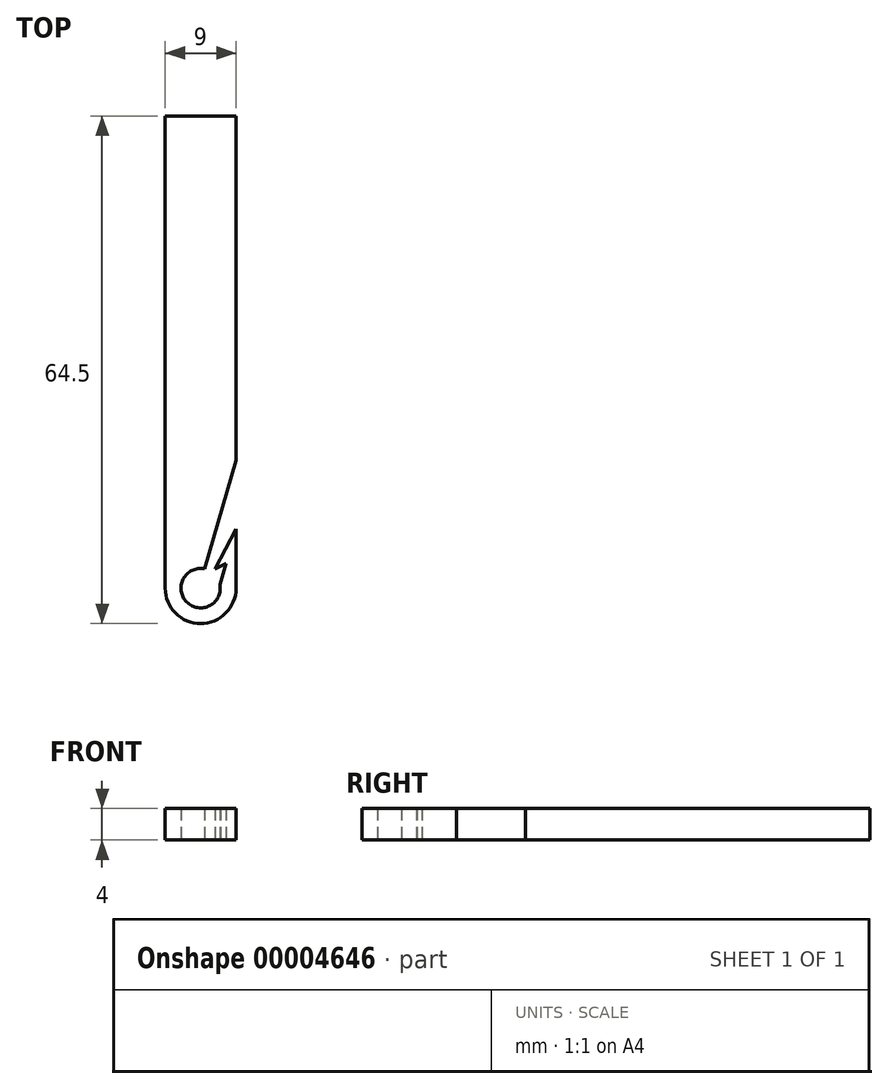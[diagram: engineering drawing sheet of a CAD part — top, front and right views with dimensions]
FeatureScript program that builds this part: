
annotation { "Feature Type Name" : "Feature", "Feature Type Description" : "" }
export const myFeature = defineFeature(function(context is Context, id is Id, definition is map)
    precondition{}
    {
        {
            var Q0;
            Q0=qCreatedBy(makeId("Top.planeOp"),FACE);
            var sketch = newSketch(context, id + "F0", { "sketchPlane" : qUnion([Q0])});
            skCircle(sketch, "E0", {"center": v(0, 0) * mm, "radius": 4.5 * mm});
            skCircle(sketch, "E1.0", {"center": v(0, 0) * mm, "radius": 2.5 * mm});
            skLineSegment(sketch, "E2", {"start": v(-4.5, 0) * mm, "end": v(-4.5, 60) * mm});
            skLineSegment(sketch, "E3", {"start": v(-4.5, 60) * mm, "end": v(4.5, 60) * mm});
            skLineSegment(sketch, "E4", {"start": v(4.5, 0) * mm, "end": v(4.5, 60) * mm});
            skLineSegment(sketch, "E5", {"start": v(0.47, 2.46) * mm, "end": v(4.5, 16.24) * mm});
            skLineSegment(sketch, "E6", {"start": v(1.8, -1.73) * mm, "end": v(4.5, 7.5) * mm});
            skLineSegment(sketch, "E7", {"start": v(3.23, 3.14) * mm, "end": v(1.8, 2.43) * mm});
            skLineSegment(sketch, "E8", {"start": v(1.8, 2.43) * mm, "end": v(4.5, 7.5) * mm});
            skSolve(sketch);
        }
        {
            var Q0;
            {var subQ6=sQuery(id+"F0.wireOp",EDGE,"E2");Q0=makeQuery(id+"F0.imprint","IMPRINT",FACE,{"disambiguationData":[TD([[makeQuery(id+"F0.imprint","IMPRINT",EDGE,{"derivedFrom":subQ6}),-1.0]])]});}
            var Q1;
            {var subQ3=sQuery(id+"F0.wireOp",EDGE,"E0");var subQ10=makeQuery(id+"F0.imprint","INTERSECT",VERTEX,{"derivedFrom":[subQ3,sQuery(id+"F0.wireOp",EDGE,"E2")]});Q1=makeQuery(id+"F0.imprint","IMPRINT",FACE,{"disambiguationData":[TD([[makeQuery(id+"F0.imprint","IMPRINT",EDGE,{"disambiguationData":[TD([[subQ10,1.0]])],"derivedFrom":subQ3}),1.0]])]});}
            var Q2;
            {var subQ1=sQuery(id+"F0.wireOp",EDGE,"E0");var subQ3=sQuery(id+"F0.wireOp",EDGE,"E4");var subQ5=makeQuery(id+"F0.imprint","INTERSECT",VERTEX,{"derivedFrom":[subQ1,subQ3]});Q2=makeQuery(id+"F0.imprint","IMPRINT",FACE,{"disambiguationData":[TD([[makeQuery(id+"F0.imprint","IMPRINT",EDGE,{"disambiguationData":[TD([[subQ5,-1.0]])],"derivedFrom":subQ1}),-1.0]])]});}
            var Q3;
            {var subQ0=sQuery(id+"F0.wireOp",EDGE,"E8");var subQ1=sQuery(id+"F0.wireOp",EDGE,"E0");var subQ2=makeQuery(id+"F0.imprint","INTERSECT",VERTEX,{"derivedFrom":[subQ1,subQ0]});Q3=makeQuery(id+"F0.imprint","IMPRINT",FACE,{"disambiguationData":[TD([[makeQuery(id+"F0.imprint","IMPRINT",EDGE,{"disambiguationData":[TD([[subQ2,1.0]])],"derivedFrom":subQ1}),-1.0]])]});}
            var Q4;
            {var subQ3=sQuery(id+"F0.wireOp",EDGE,"E7");Q4=makeQuery(id+"F0.imprint","IMPRINT",FACE,{"disambiguationData":[TD([[makeQuery(id+"F0.imprint","IMPRINT",EDGE,{"derivedFrom":subQ3}),-1.0]])]});}
            extrude(context, id + "F1", {"entities" : qUnion([Q0, Q1, Q2, Q3, Q4]), "depth" : 4 * mm});
        }
        {
            var Q0;
            Q0=makeQuery(id+"F1.opExtrude","SWEPT_FACE",FACE,{"disambiguationData":[OSD([sQuery(id+"F0.wireOp",EDGE,"E3")])]});
            var sketch = newSketch(context, id + "F2", { "sketchPlane" : qUnion([Q0])});
            skLineSegment(sketch, "E9.0", {"start": v(4.5, 4) * mm, "end": v(-4.5, 4) * mm});
            skLineSegment(sketch, "E10.0", {"start": v(-4.5, 4) * mm, "end": v(-4.5, 0) * mm});
            skLineSegment(sketch, "E11.0", {"start": v(4.5, 0) * mm, "end": v(-4.5, 0) * mm});
            skLineSegment(sketch, "E12.0", {"start": v(4.5, 4) * mm, "end": v(4.5, 0) * mm});
            skLineSegment(sketch, "E13.0", {"start": v(5, 4.5) * mm, "end": v(-5, 4.5) * mm});
            skLineSegment(sketch, "E13.1", {"start": v(5, 4.5) * mm, "end": v(5, -0.5) * mm});
            skLineSegment(sketch, "E13.2", {"start": v(5, -0.5) * mm, "end": v(-5, -0.5) * mm});
            skLineSegment(sketch, "E13.3", {"start": v(-5, 4.5) * mm, "end": v(-5, -0.5) * mm});
            skLineSegment(sketch, "E14.0", {"start": v(6, 5.5) * mm, "end": v(-6, 5.5) * mm});
            skLineSegment(sketch, "E14.1", {"start": v(6, 5.5) * mm, "end": v(6, -1.5) * mm});
            skLineSegment(sketch, "E14.2", {"start": v(6, -1.5) * mm, "end": v(-6, -1.5) * mm});
            skLineSegment(sketch, "E14.3", {"start": v(-6, 5.5) * mm, "end": v(-6, -1.5) * mm});
            skSolve(sketch);
        }
        {
            var Q0;
            Q0=makeQuery(id+"F2.imprint","IMPRINT",FACE,{"disambiguationData":[TD([[makeQuery(id+"F2.imprint","IMPRINT",EDGE,{"derivedFrom":sQuery(id+"F2.wireOp",EDGE,"E13.0")}),-1.0]])]});
            extrude(context, id + "F3", {"entities" : qUnion([Q0]), "oppositeDirection" : true, "depth" : 9 * mm});
        }
        {
            var Q0;
            Q0=makeQuery(id+"F3.opExtrude","SWEPT_FACE",FACE,{"disambiguationData":[OSD([sQuery(id+"F2.wireOp",EDGE,"E14.3")])]});
            var Q1;
            Q1=makeQuery(id+"F3.opExtrude","SWEPT_FACE",FACE,{"disambiguationData":[OSD([sQuery(id+"F2.wireOp",EDGE,"E14.2")])]});
            var Q2;
            Q2=makeQuery(id+"F3.opExtrude","SWEPT_FACE",FACE,{"disambiguationData":[OSD([sQuery(id+"F2.wireOp",EDGE,"E14.1")])]});
            var Q3;
            Q3=makeQuery(id+"F3.opExtrude","SWEPT_FACE",FACE,{"disambiguationData":[OSD([sQuery(id+"F2.wireOp",EDGE,"E14.0")])]});
            fillet(context, id + "F4", {"entities" : qUnion([Q0, Q1, Q2, Q3]), "radius" : 1 * mm, "tangentPropagation" : true, "allowEdgeOverflow" : false});
        }
        {
            var Q0;
            Q0=makeQuery(id+"F3.opExtrude","SWEPT_BODY",BODY,{"disambiguationData":[OSD([sQuery(id+"F2.wireOp",EDGE,"E13.0"),sQuery(id+"F2.wireOp",EDGE,"E13.1"),sQuery(id+"F2.wireOp",EDGE,"E13.2"),sQuery(id+"F2.wireOp",EDGE,"E13.3"),sQuery(id+"F2.wireOp",EDGE,"E14.0"),sQuery(id+"F2.wireOp",EDGE,"E14.1"),sQuery(id+"F2.wireOp",EDGE,"E14.2"),sQuery(id+"F2.wireOp",EDGE,"E14.3")])]});
            deleteBodies(context, id + "F5", {"entities" : qUnion([Q0])});
        }
    });
